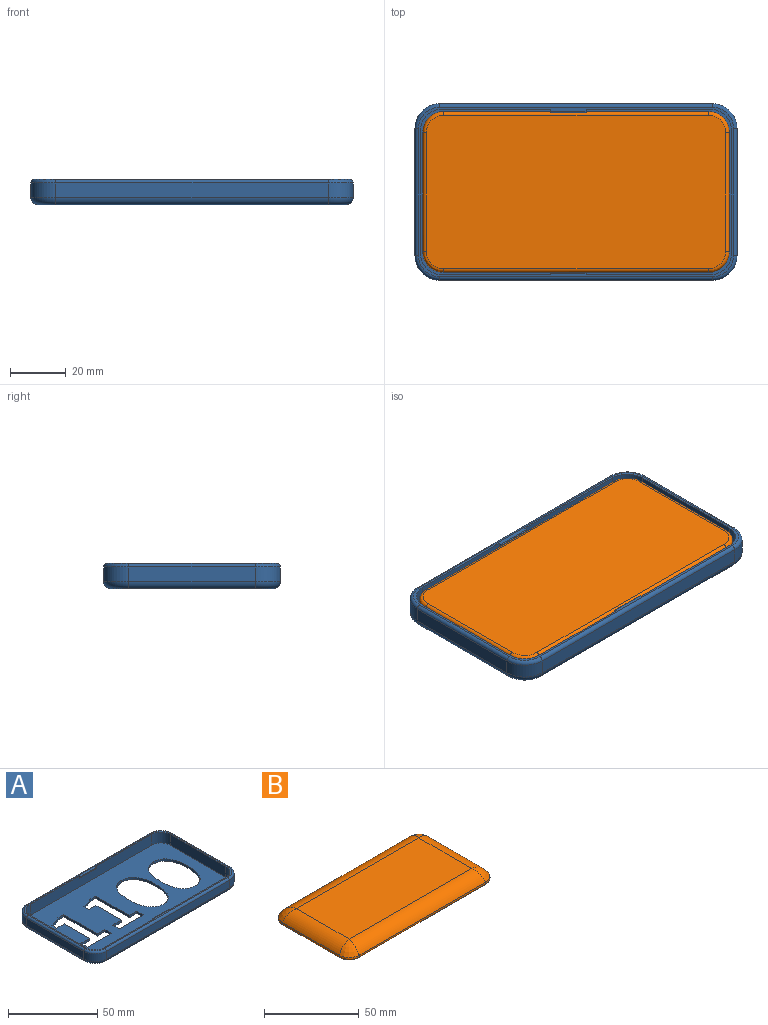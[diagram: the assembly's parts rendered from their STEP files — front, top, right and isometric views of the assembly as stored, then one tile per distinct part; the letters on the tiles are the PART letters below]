
ASSEMBLY  parts=2 mates=1
PART A: 76 faces, bbox 116.8x64.7x9 mm
  f0: plane 110.22x58.12mm, normal (0,0,-1), area 4628.3mm2, adj f30,f31,f32,f33,f34,f35,f36,f37
  f1: plane 111.3x59.2mm, normal (0,0,1), area 4796.1mm2, adj f2,f10,f11,f12,f13,f14,f15,f16
  f2: plane 96.06x7.5mm, normal (0,1,0), area 702.7mm2, adj f1,f10,f16,f18,f24,f25,f27
  f3: cylinder r=8.89mm len=8.89mm, axis (0,0,-1), area 72.5mm2, adj f4,f17,f34,f40
  f4: plane 97.52x5.19mm, normal (0,-1,0), area 506.1mm2, adj f3,f5,f32,f42
  f5: cylinder r=8.89mm len=8.89mm, axis (0,0,-1), area 72.5mm2, adj f4,f6,f30,f44
  f6: plane 45.42x5.19mm, normal (1,0,0), area 235.7mm2, adj f5,f7,f31,f45
  f7: cylinder r=8.89mm len=8.89mm, axis (0,0,-1), area 72.5mm2, adj f6,f8,f33,f43
  f8: plane 97.52x5.19mm, normal (0,1,0), area 506.1mm2, adj f7,f9,f35,f41
  f9: cylinder r=8.89mm len=8.89mm, axis (0,0,-1), area 72.5mm2, adj f8,f17,f37,f39
  f10: cylinder r=7.62mm len=7.62mm, axis (0,0,-1), area 89.8mm2, adj f1,f2,f11,f18
  f11: plane 43.96x7.5mm, normal (1,0,0), area 329.7mm2, adj f1,f10,f12,f18
  f12: cylinder r=7.62mm len=7.62mm, axis (0,0,-1), area 89.8mm2, adj f1,f11,f13,f18
  f13: plane 96.06x7.5mm, normal (0,-1,0), area 702.7mm2, adj f1,f12,f14,f18,f19,f20,f22
  f14: cylinder r=7.62mm len=7.62mm, axis (0,0,-1), area 89.8mm2, adj f1,f13,f15,f18
  f15: plane 43.96x7.5mm, normal (-1,0,0), area 329.7mm2, adj f1,f14,f16,f18
  f16: cylinder r=7.62mm len=7.62mm, axis (0,0,-1), area 89.8mm2, adj f1,f2,f15,f18
  f17: plane 45.42x5.19mm, normal (-1,0,0), area 235.7mm2, adj f3,f9,f36,f38
  f18: plane 112.76x60.66mm, normal (0,0,1), area 269.4mm2, adj f2,f10,f11,f12,f13,f14,f15,f16
  f19: plane 1.4x1.27mm, normal (1,0,0), area 1.1mm2, adj f13,f18,f21,f22,f23
  f20: plane 1.4x1.27mm, normal (-1,0,0), area 1.1mm2, adj f13,f18,f21,f22,f23
  f21: cylinder r=0.76mm len=12.7mm, axis (-1,0,0), area 15.2mm2, adj f19,f20,f22,f23
  f22: plane 12.7x0.51mm, normal (0,-0.71,-0.71), area 9.1mm2, adj f13,f19,f20,f21
  f23: cylinder r=0.51mm len=12.7mm, axis (1,0,0), area 4.7mm2, adj f18,f19,f20,f21
  f24: plane 1.4x0.76mm, normal (1,0,0), area 0.7mm2, adj f2,f18,f26,f27,f28,f29
  f25: plane 1.4x0.76mm, normal (-1,0,0), area 0.7mm2, adj f2,f18,f26,f27,f28,f29
  f26: plane 12.7x0.07mm, normal (0,1,0), area 0.9mm2, adj f24,f25,f28,f29
  f27: plane 12.7x0.51mm, normal (0,0.71,-0.71), area 9.1mm2, adj f2,f24,f25,f28
  f28: cylinder r=0.76mm len=12.7mm, axis (1,0,0), area 8.1mm2, adj f24,f25,f26,f27
  f29: cylinder r=0.25mm len=12.7mm, axis (1,0,0), area 5.1mm2, adj f18,f24,f25,f26
  f30: torus R=6.35mm, axis (0,0,1), area 49.9mm2, adj f0,f5,f31,f32
  f31: cylinder r=2.54mm len=45.42mm, axis (0,1,0), area 181.2mm2, adj f0,f6,f30,f33
  f32: cylinder r=2.54mm len=97.52mm, axis (1,0,0), area 389.1mm2, adj f0,f4,f30,f34
  f33: torus R=6.35mm, axis (0,0,1), area 49.9mm2, adj f0,f7,f31,f35
  f34: torus R=6.35mm, axis (0,0,1), area 49.9mm2, adj f0,f3,f32,f36
  f35: cylinder r=2.54mm len=97.52mm, axis (-1,0,0), area 389.1mm2, adj f0,f8,f33,f37
  f36: cylinder r=2.54mm len=45.42mm, axis (0,-1,0), area 181.2mm2, adj f0,f17,f34,f37
  f37: torus R=6.35mm, axis (0,0,1), area 49.9mm2, adj f0,f9,f35,f36
  f38: cylinder r=1.27mm len=45.42mm, axis (0,1,0), area 90.6mm2, adj f17,f18,f39,f40
  f39: torus R=7.62mm, axis (0,0,1), area 26.4mm2, adj f9,f18,f38,f41
  f40: torus R=7.62mm, axis (0,0,1), area 26.4mm2, adj f3,f18,f38,f42
  f41: cylinder r=1.27mm len=97.52mm, axis (1,0,0), area 194.5mm2, adj f8,f18,f39,f43
  f42: cylinder r=1.27mm len=97.52mm, axis (-1,0,0), area 194.5mm2, adj f4,f18,f40,f44
  f43: torus R=7.62mm, axis (0,0,1), area 26.4mm2, adj f7,f18,f41,f45
  f44: torus R=7.62mm, axis (0,0,1), area 26.4mm2, adj f5,f18,f42,f45
  f45: cylinder r=1.27mm len=45.42mm, axis (0,-1,0), area 90.6mm2, adj f6,f18,f43,f44
  f46: extruded ~16.34x10.76mm, area 33mm2, adj f0,f1,f47,f49
  f47: extruded ~16.6x10.76mm, area 33.3mm2, adj f0,f1,f46,f48
  f48: extruded ~16.6x10.72mm, area 33.2mm2, adj f0,f1,f47,f49
  f49: extruded ~16.34x10.72mm, area 32.9mm2, adj f0,f1,f46,f48
  f50: extruded ~16.34x10.76mm, area 33mm2, adj f0,f1,f51,f53
  f51: extruded ~16.6x10.76mm, area 33.3mm2, adj f0,f1,f50,f52
  f52: extruded ~16.6x10.72mm, area 33.2mm2, adj f0,f1,f51,f53
  f53: extruded ~16.34x10.72mm, area 32.9mm2, adj f0,f1,f50,f52
  f54: plane 6.82x1.5mm, normal (0,-1,0), area 10.2mm2, adj f0,f1,f55,f64
  f55: plane 5.11x1.5mm, normal (1,0,0), area 7.7mm2, adj f0,f1,f54,f56
  f56: plane 19.09x1.5mm, normal (0,1,0), area 28.6mm2, adj f0,f1,f55,f57
  f57: plane 5.11x1.5mm, normal (-1,0,0), area 7.7mm2, adj f0,f1,f56,f58
  f58: plane 5.96x1.5mm, normal (0,-1,0), area 8.9mm2, adj f0,f1,f57,f59
  f59: plane 26.63x1.5mm, normal (-1,0,0), area 39.9mm2, adj f0,f1,f58,f60
  f60: plane 4.67x1.5mm, normal (0,-1,0), area 7mm2, adj f0,f1,f59,f61
  f61: extruded ~7.38x2.66mm, area 11.8mm2, adj f0,f1,f60,f62
  f62: plane 3.9x1.5mm, normal (1,0,0), area 5.9mm2, adj f0,f1,f61,f63
  f63: plane 5.74x1.5mm, normal (0,1,0), area 8.6mm2, adj f0,f1,f62,f64
  f64: plane 20.07x1.5mm, normal (1,0,0), area 30.1mm2, adj f0,f1,f54,f63
  f65: plane 6.82x1.5mm, normal (0,-1,0), area 10.2mm2, adj f0,f1,f66,f75
  f66: plane 5.11x1.5mm, normal (1,0,0), area 7.7mm2, adj f0,f1,f65,f67
  f67: plane 19.09x1.5mm, normal (0,1,0), area 28.6mm2, adj f0,f1,f66,f68
  f68: plane 5.11x1.5mm, normal (-1,0,0), area 7.7mm2, adj f0,f1,f67,f69
  f69: plane 5.96x1.5mm, normal (0,-1,0), area 8.9mm2, adj f0,f1,f68,f70
  f70: plane 26.63x1.5mm, normal (-1,0,0), area 39.9mm2, adj f0,f1,f69,f71
  f71: plane 4.67x1.5mm, normal (0,-1,0), area 7mm2, adj f0,f1,f70,f72
  f72: extruded ~7.38x2.66mm, area 11.8mm2, adj f0,f1,f71,f73
  f73: plane 3.9x1.5mm, normal (1,0,0), area 5.9mm2, adj f0,f1,f72,f74
  f74: plane 5.74x1.5mm, normal (0,1,0), area 8.6mm2, adj f0,f1,f73,f75
  f75: plane 20.07x1.5mm, normal (1,0,0), area 30.1mm2, adj f0,f1,f65,f74
PART B: 18 faces, bbox 111.4x59.3x7.2 mm
  f0: plane 91.46x39.36mm, normal (0,0,1), area 3600.1mm2, adj f2,f5,f6,f9
  f1: plane 107.1x55mm, normal (0,0,-1), area 5857.6mm2, adj f10,f11,f12,f13,f14,f15,f16,f17
  f2: cylinder r=10.16mm len=42.52mm, axis (0,-1,0), area 447.1mm2, adj f0,f3,f4,f15
  f3: bspline ~9.36x9.36mm, area 69.5mm2, adj f2,f5,f17
  f4: bspline ~9.36x9.36mm, area 69.5mm2, adj f2,f6,f13
  f5: cylinder r=10.16mm len=94.62mm, axis (1,0,0), area 1016.1mm2, adj f0,f3,f7,f16
  f6: cylinder r=10.16mm len=94.62mm, axis (1,0,0), area 1016.1mm2, adj f0,f4,f8,f11
  f7: bspline ~9.36x9.36mm, area 69.5mm2, adj f5,f9,f14
  f8: bspline ~9.36x9.36mm, area 69.5mm2, adj f6,f9,f10
  f9: cylinder r=10.16mm len=42.52mm, axis (0,-1,0), area 447.1mm2, adj f0,f7,f8,f12
  f10: bspline ~8.96x8.96mm, area 29.9mm2, adj f1,f8,f11,f12
  f11: cylinder r=1.27mm len=94.62mm, axis (1,0,0), area 248.4mm2, adj f1,f6,f10,f13
  f12: cylinder r=1.27mm len=42.52mm, axis (0,-1,0), area 111.6mm2, adj f1,f9,f10,f14
  f13: bspline ~8.96x8.96mm, area 29.9mm2, adj f1,f4,f11,f15
  f14: bspline ~8.96x8.96mm, area 29.9mm2, adj f1,f7,f12,f16
  f15: cylinder r=1.27mm len=42.52mm, axis (0,-1,0), area 111.6mm2, adj f1,f2,f13,f17
  f16: cylinder r=1.27mm len=94.62mm, axis (1,0,0), area 248.4mm2, adj f1,f5,f14,f17
  f17: bspline ~8.96x8.96mm, area 29.9mm2, adj f1,f3,f15,f16
PLACE A t=(-3.6,10.76,13.22)mm fixed
PLACE B rot(axis=(1,0,0),180deg) t=(-3.6,10.76,21.92)mm
MATE planar A.f1 <-> B.f0  axis (0,0,1) through (8.76,11.68,14.72)mm
